# Revit family: Edge_TB42_E_Top_Hung_Standard
name_source: partatom
category: Windows
revit_build: Autodesk Revit 2014 (Build: 20130308_1515(x64)
units: mm (PartAtom-declared; Revit-internal decimal feet)

## types (6) — shared parameters
Aluminium Thickness = 1 mm  [stored 0.00328084 ft]
Area Pane Left Bottom = 0.13 m²
Area Pane Left Top = 0.23 m²
Bead SG Gap = 13 mm
Bottom Hung = No
Casement Dimension = 42 mm  [stored 0.137795 ft]
Custom Sash Height = 554 mm  [stored 1.81759 ft]
Custom Sash Width = 554 mm  [stored 1.81759 ft]
Custom Window Height = 890 mm  [stored 2.91995 ft]
DG Extrusion Start = 11 mm  [stored 0.0360892 ft]
DG Gasket Finish = Double Glazing Gasket Material
DG Thickness Calc = 4 mm  [stored 0.0131234 ft]
Default Sill Height = 800 mm  [stored 2.62467 ft]
Depth Bead = 28 mm  [stored 0.0918635 ft]
Description = Thermal break casement windows (42mm), Type E top hung
Frame Center Offset = 21 mm  [stored 0.0688976 ft]
Has Stiffener Cap = No
Height = 890 mm  [stored 2.91995 ft]
Height Fixed Pane Bottom LHS = 260 mm  [stored 0.853018 ft]
Height Fixed Pane RHS = 830 mm  [stored 2.7231 ft]
Height Panel 1 = 539 mm  [stored 1.76837 ft]
Height Sash = 524 mm  [stored 1.71916 ft]
Height Sash Opening = 554 mm  [stored 1.81759 ft]
Length Mullion = 890 mm  [stored 2.91995 ft]
Length Transom = 540 mm  [stored 1.77165 ft]
Limit Fixed Pane Height Max = 1800 mm  [stored 5.90551 ft]
Limit Fixed Pane Height Min = 200 mm  [stored 0.656168 ft]
Limit Fixed Pane Width Max = 1500 mm  [stored 4.92126 ft]
Limit Fixed Pane Width Min = 200 mm  [stored 0.656168 ft]
Limit Sash Height Max = 1200 mm
Limit Sash Height Min = 300 mm  [stored 0.984252 ft]
Limit Sash Width Max = 1500 mm  [stored 4.92126 ft]
Limit Sash Width Min = 300 mm  [stored 0.984252 ft]
Limit Window Height Max = 1860 mm  [stored 6.10236 ft]
Limit Window Height Min = 830 mm  [stored 2.7231 ft]
Limit Window Width Max = 2130 mm  [stored 6.98819 ft]
Limit Window Width Min = 830 mm  [stored 2.7231 ft]
Manufacturer = Crealco
Max System DG One Piece Thickness = 6 mm  [stored 0.019685 ft]
Max System DG Unit Thickness = 25 mm  [stored 0.082021 ft]
Model = Edge
Offset Bead SG Center Reversed = 21 mm  [stored 0.0688976 ft]
Offset Mullion Left = 570 mm  [stored 1.87008 ft]
Offset Panel 3 Bead Top = 600 mm  [stored 1.9685 ft]
Offset Panel 4 Left = 600 mm  [stored 1.9685 ft]
Offset Sash Left = 23 mm  [stored 0.0754593 ft]
Offset Sash Top = 23 mm  [stored 0.0754593 ft]
Offset Transom Top = 570 mm  [stored 1.87008 ft]
Offset Window Exterior = 21 mm  [stored 0.0688976 ft]
SG Gasket Thickness = 6 mm  [stored 0.019685 ft]
Sash Center Offset = 18 mm
Sash Overlap = 7 mm  [stored 0.0229659 ft]
Sash Spacing Inner = 8 mm  [stored 0.0262467 ft]
Top Hung = Yes
URL = http://www.crealco.co.za
Wall Closure = By host
Width Bead = 15 mm  [stored 0.0492126 ft]
Width Fixed Pane Bottom LHS = 540 mm  [stored 1.77165 ft]
Width Panel 1 = 540 mm  [stored 1.77165 ft]
Width Profile = 30 mm  [stored 0.0984252 ft]
Width Sash = 524 mm  [stored 1.71916 ft]
Width Sash Opening = 554 mm  [stored 1.81759 ft]
zero-valued in all types: Depth Mullion, Mullion Depth Windload Based, Window Exterior Offset

## per-type parameters (varying)
| type | Area Pane Right | Clearvue Insulated LowE SHGC Value | Clearvue Insulated LowE U Value | Clearvue Insulated SHGC Value | Clearvue Insulated U Value | Clearvue SHGC Value | Clearvue U Value | Custom Windload | Custom Window Width | Energy Advantage SHGC Value | Energy Advantage U Value | Intruderprufe Insulated LowE SHGC Value | Intruderprufe Insulated LowE U Value | Intruderprufe Insulated SHGC Value | Intruderprufe Insulated U Value | Intruderprufe LowE SHGC Value | Intruderprufe LowE U Value | Intruderprufe SHGC Value | Intruderprufe U Value | Max Pane Area | Width | Width Fixed Pane RHS | Windload Design |
| EDGE-1209T-1000Pa | 0.45 m² | 0.558 | 3.14 | 0.613 | 3.71 | 0.678 | 6.49 | 1000 mm  [stored 3.28084 ft] | 1190 mm  [stored 3.9042 ft] | 0.607 | 4.85 | 0.509 | 3.09 | 0.561 | 3.67 | 0.566 | 4.86 | 0.631 | 6.37 | 0.45 m² | 1190 mm  [stored 3.9042 ft] | 560 mm | 1000 mm  [stored 3.28084 ft] |
| EDGE-1509T-1000Pa | 0.7 m² | 0.62 | 3.16 | 0.681 | 3.81 | 0.756 | 6.85 | 1000 mm  [stored 3.28084 ft] | 1490 mm  [stored 4.88845 ft] | 0.676 | 5 | 0.565 | 3.1 | 0.625 | 3.76 | 0.63 | 5 | 0.705 | 6.73 | 0.7 m² | 1490 mm  [stored 4.88845 ft] | 860 mm  [stored 2.82152 ft] | 1000 mm  [stored 3.28084 ft] |
| EDGE-1209T-1500Pa | 0.45 m² | 0.558 | 3.14 | 0.613 | 3.71 | 0.678 | 6.49 | 1500 mm  [stored 4.92126 ft] | 1190 mm  [stored 3.9042 ft] | 0.607 | 4.85 | 0.509 | 3.09 | 0.561 | 3.67 | 0.566 | 4.86 | 0.631 | 6.37 | 0.45 m² | 1190 mm  [stored 3.9042 ft] | 560 mm | 1500 mm  [stored 4.92126 ft] |
| EDGE-1209T-2000Pa | 0.45 m² | 0.558 | 3.14 | 0.613 | 3.71 | 0.678 | 6.49 | 2000 mm  [stored 6.56168 ft] | 1190 mm  [stored 3.9042 ft] | 0.607 | 4.85 | 0.509 | 3.09 | 0.561 | 3.67 | 0.566 | 4.86 | 0.631 | 6.37 | 0.45 m² | 1190 mm  [stored 3.9042 ft] | 560 mm | 2000 mm  [stored 6.56168 ft] |
| EDGE-1509T-1500Pa | 0.7 m² | 0.62 | 3.16 | 0.681 | 3.81 | 0.756 | 6.85 | 1500 mm  [stored 4.92126 ft] | 1490 mm  [stored 4.88845 ft] | 0.676 | 5 | 0.565 | 3.1 | 0.625 | 3.76 | 0.63 | 5 | 0.705 | 6.73 | 0.7 m² | 1490 mm  [stored 4.88845 ft] | 860 mm  [stored 2.82152 ft] | 1500 mm  [stored 4.92126 ft] |
| EDGE-1509T-2000Pa | 0.7 m² | 0.62 | 3.16 | 0.681 | 3.81 | 0.756 | 6.85 | 2000 mm  [stored 6.56168 ft] | 1490 mm  [stored 4.88845 ft] | 0.676 | 5 | 0.565 | 3.1 | 0.625 | 3.76 | 0.63 | 5 | 0.705 | 6.73 | 0.7 m² | 1490 mm  [stored 4.88845 ft] | 860 mm  [stored 2.82152 ft] | 2000 mm  [stored 6.56168 ft] |

note: [stored X ft] marks values corroborated as IEEE doubles in the binary element streams (Revit-internal decimal feet)

## geometry (parser evidence)
native form markers: Extrusion x1, Sweep x30
no freeform markers — native parametric forms only
